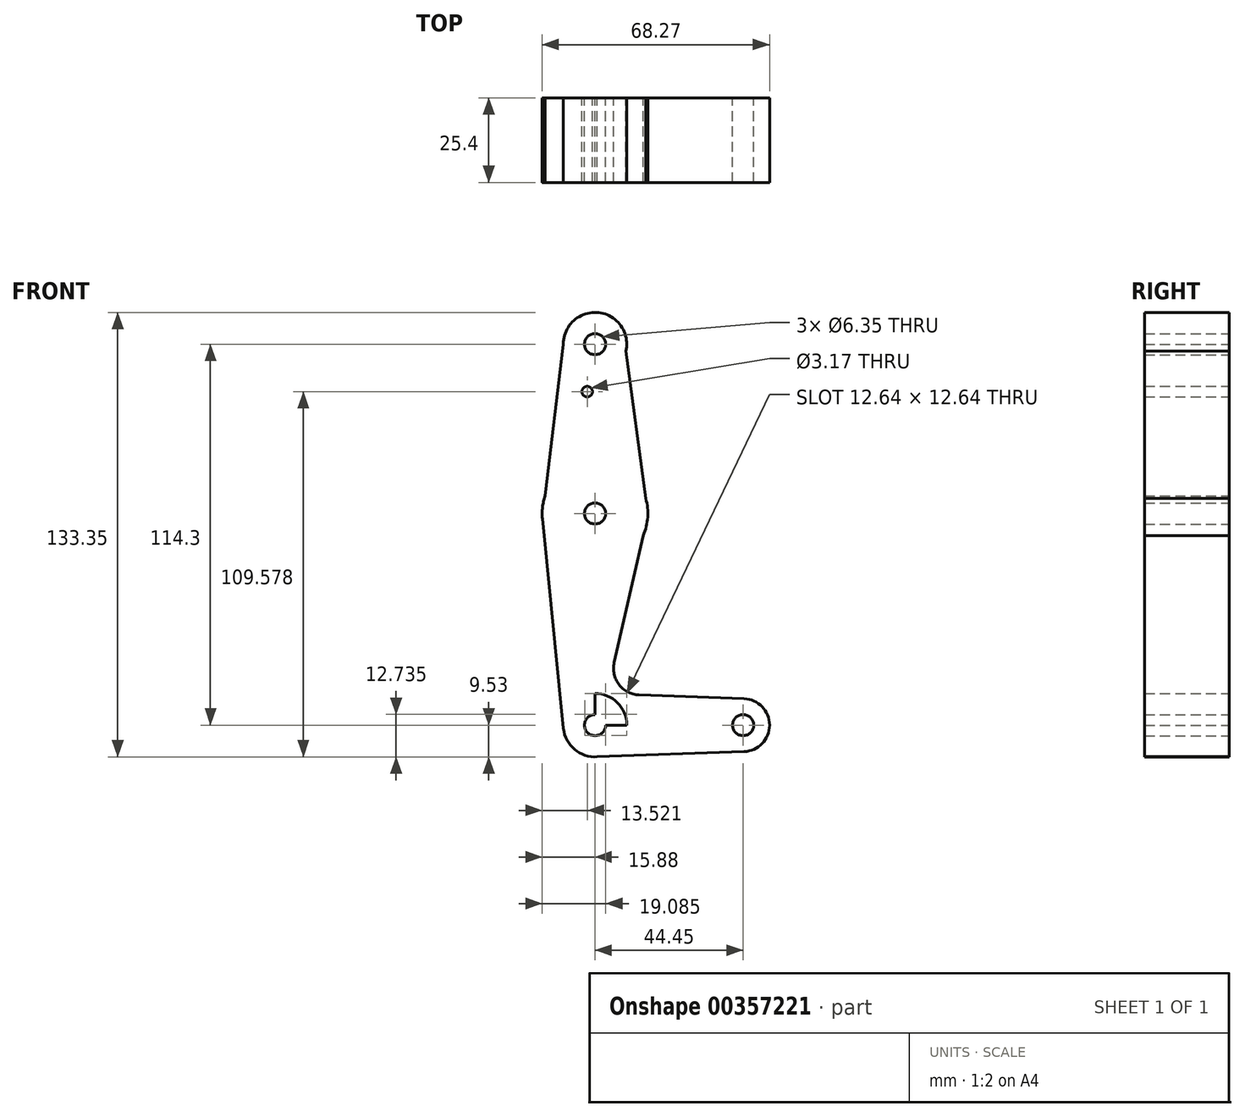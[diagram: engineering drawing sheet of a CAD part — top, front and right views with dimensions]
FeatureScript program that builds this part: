
annotation { "Feature Type Name" : "Feature", "Feature Type Description" : "" }
export const myFeature = defineFeature(function(context is Context, id is Id, definition is map)
    precondition{}
    {
        {
            var Q0;
            Q0=qCreatedBy(makeId("Front.planeOp"),FACE);
            var sketch = newSketch(context, id + "F0", { "sketchPlane" : qUnion([Q0])});
            skCircle(sketch, "E0", {"center": v(0, 0) * mm, "radius": 9.53 * mm});
            skCircle(sketch, "E1", {"center": v(0, 63.5) * mm, "radius": 15.88 * mm});
            skCircle(sketch, "E2", {"center": v(0, 114.3) * mm, "radius": 9.53 * mm});
            skCircle(sketch, "E3", {"center": v(44.45, 0) * mm, "radius": 7.94 * mm});
            skLineSegment(sketch, "E4", {"start": v(0, 0) * mm, "end": v(0, 63.5) * mm});
            skLineSegment(sketch, "E5", {"start": v(0, 114.3) * mm, "end": v(0, 63.5) * mm});
            skLineSegment(sketch, "E6", {"start": v(0, 0) * mm, "end": v(44.45, 0) * mm});
            skLineSegment(sketch, "E7", {"start": v(0, 114.3) * mm, "end": v(0, 0) * mm});
            skLineSegment(sketch, "E8", {"start": v(0, 63.5) * mm, "end": v(0, 114.3) * mm});
            skLineSegment(sketch, "E9", {"start": v(9.28, 112.17) * mm, "end": v(15.87, 63.18) * mm});
            skLineSegment(sketch, "E10", {"start": v(-9.26, 116.54) * mm, "end": v(-15.8, 61.91) * mm});
            skLineSegment(sketch, "E11", {"start": v(15.87, 63.18) * mm, "end": v(5.74, 18.77) * mm});
            skLineSegment(sketch, "E12", {"start": v(13.21, 9.05) * mm, "end": v(44.73, 7.93) * mm});
            skLineSegment(sketch, "E13", {"start": v(0, -9.53) * mm, "end": v(44.73, -7.93) * mm});
            skLineSegment(sketch, "E14", {"start": v(-9.48, -0.95) * mm, "end": v(-15.8, 61.91) * mm});
            skCircle(sketch, "E15", {"center": v(0, 114.3) * mm, "radius": 3.18 * mm});
            skCircle(sketch, "E16", {"center": v(0, 63.5) * mm, "radius": 3.18 * mm});
            skCircle(sketch, "E17", {"center": v(0, 0) * mm, "radius": 3.18 * mm});
            skCircle(sketch, "E18", {"center": v(44.45, 0) * mm, "radius": 3.18 * mm});
            skPoint(sketch, "E19.newPointA", {"position": v(1.25, -0.95) * mm});
            skArc(sketch, "E19.filletArc", {"start": v(5.74, 18.77) * mm, "mid": v(7.2, 12.15) * mm, "end": v(13.21, 9.05) * mm});
            skCircle(sketch, "E20", {"center": v(-2.36, 100.05) * mm, "radius": 1.59 * mm});
            skLineSegment(sketch, "E21", {"start": v(0, 100.03) * mm, "end": v(0, 63.5) * mm});
            skSolve(sketch);
        }
        {
            var Q0;
            Q0 = qSketchRegion(id + "F0", true);
            extrude(context, id + "F1", {"entities" : qUnion([Q0]), "depth" : 25.4 * mm});
        }
    });
